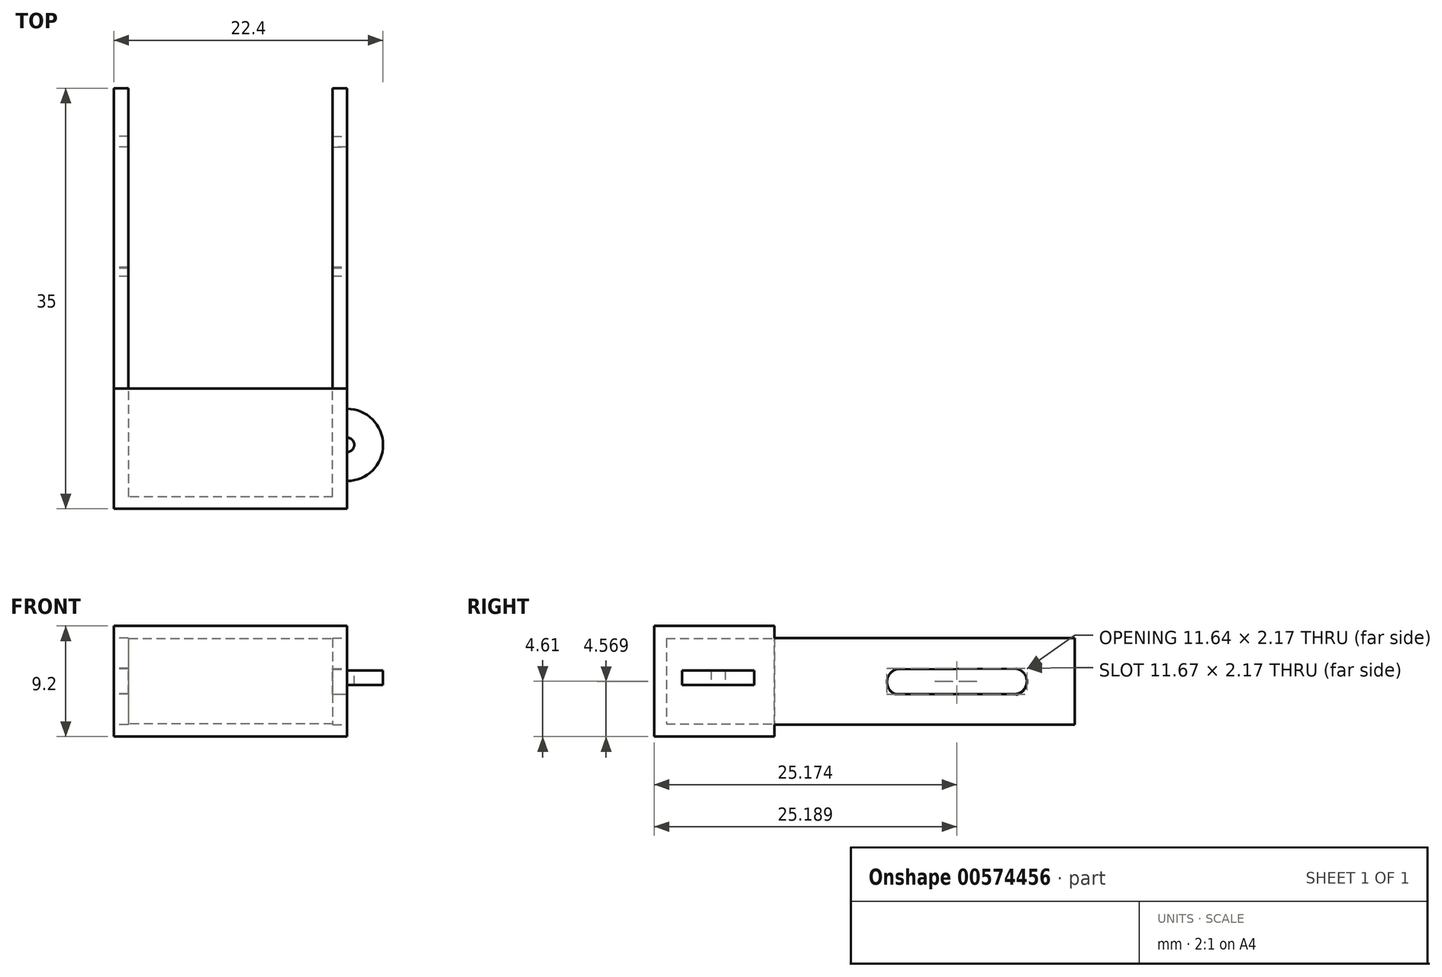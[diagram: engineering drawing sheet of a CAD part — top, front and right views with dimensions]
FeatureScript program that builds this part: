
annotation { "Feature Type Name" : "Feature", "Feature Type Description" : "" }
export const myFeature = defineFeature(function(context is Context, id is Id, definition is map)
    precondition{}
    {
        {
            var Q0;
            Q0=qCreatedBy(makeId("Right.planeOp"),FACE);
            var sketch = newSketch(context, id + "F0", { "sketchPlane" : qUnion([Q0])});
            skLineSegment(sketch, "E0.bottom", {"start": v(-18.67, 6.84) * mm, "end": v(-8.67, 6.84) * mm});
            skLineSegment(sketch, "E0.top", {"start": v(-18.67, -2.36) * mm, "end": v(-8.67, -2.36) * mm});
            skLineSegment(sketch, "E0.left", {"start": v(-18.67, 6.84) * mm, "end": v(-18.67, -2.36) * mm});
            skLineSegment(sketch, "E0.right", {"start": v(-8.67, 6.84) * mm, "end": v(-8.67, -2.36) * mm});
            skPoint(sketch, "E1", {"position": v(-8.67, 2.24) * mm});
            skLineSegment(sketch, "E2", {"start": v(-8.67, 2.24) * mm, "end": v(-8.67, 5.84) * mm});
            skLineSegment(sketch, "E3", {"start": v(-8.67, 5.84) * mm, "end": v(16.33, 5.84) * mm});
            skLineSegment(sketch, "E4", {"start": v(16.33, 5.84) * mm, "end": v(16.33, -1.36) * mm});
            skLineSegment(sketch, "E5", {"start": v(16.33, -1.36) * mm, "end": v(-8.67, -1.36) * mm});
            skPoint(sketch, "E6", {"position": v(11.33, 2.27) * mm});
            skPoint(sketch, "E7", {"position": v(1.33, 2.27) * mm});
            skLineSegment(sketch, "E8", {"start": v(1.44, 3.27) * mm, "end": v(11.43, 3.33) * mm});
            skLineSegment(sketch, "E9", {"start": v(11.43, 3.33) * mm, "end": v(11.43, 1.17) * mm});
            skLineSegment(sketch, "E10", {"start": v(11.43, 1.17) * mm, "end": v(1.33, 1.2) * mm});
            skArc(sketch, "E11", {"start": v(1.44, 3.27) * mm, "mid": v(0.67, 2.28) * mm, "end": v(1.33, 1.2) * mm});
            skArc(sketch, "E12", {"start": v(11.43, 1.17) * mm, "mid": v(12.34, 2.25) * mm, "end": v(11.43, 3.33) * mm});
            skLineSegment(sketch, "E13.top", {"start": v(-8.67, -1.36) * mm, "end": v(16.33, -1.36) * mm});
            skLineSegment(sketch, "E13.left", {"start": v(-8.67, 6.84) * mm, "end": v(-8.67, -1.36) * mm});
            skSolve(sketch);
        }
        {
            var Q0;
            {var subQ1=sQuery(id+"F0.wireOp",EDGE,"E0.bottom");Q0=makeQuery(id+"F0.imprint","IMPRINT",FACE,{"disambiguationData":[TD([[makeQuery(id+"F0.imprint","IMPRINT",EDGE,{"derivedFrom":subQ1}),-1.0]])]});}
            extrude(context, id + "F1", {"entities" : qUnion([Q0]), "depth" : 19.4 * mm, "offsetDistance" : 25 * mm});
        }
        {
            var Q0;
            Q0 = qSketchRegion(id + "F0", true);
            extrude(context, id + "F2", {"entities" : qUnion([Q0]), "operationType" : NewBodyOperationType.ADD, "depth" : 1.2 * mm, "offsetDistance" : 25 * mm});
        }
        {
            var Q0;
            Q0=makeQuery(id+"F1.opExtrude","CAP_FACE",FACE,{"disambiguationData":[OSD([sQuery(id+"F0.wireOp",EDGE,"E0.bottom"),sQuery(id+"F0.wireOp",EDGE,"E0.top"),sQuery(id+"F0.wireOp",EDGE,"E0.left"),sQuery(id+"F0.wireOp",EDGE,"E0.right"),sQuery(id+"F0.wireOp",EDGE,"E13.left")])],"isStart":false});
            var sketch = newSketch(context, id + "F3", { "sketchPlane" : qUnion([Q0])});
            skPoint(sketch, "E14", {"position": v(-8.67, 6.84) * mm});
            skPoint(sketch, "E15", {"position": v(-8.67, 5.84) * mm});
            skLineSegment(sketch, "E16", {"start": v(-8.67, 5.84) * mm, "end": v(16.33, 5.84) * mm});
            skLineSegment(sketch, "E17", {"start": v(16.33, 5.84) * mm, "end": v(16.33, -1.36) * mm});
            skLineSegment(sketch, "E18", {"start": v(16.33, -1.36) * mm, "end": v(-8.67, -1.36) * mm});
            skLineSegment(sketch, "E19", {"start": v(-8.67, -1.36) * mm, "end": v(-8.67, 5.84) * mm});
            skPoint(sketch, "E20", {"position": v(10.79, 2.26) * mm});
            skPoint(sketch, "E21", {"position": v(1.25, 2.26) * mm});
            skLineSegment(sketch, "E22", {"start": v(1.47, 3.23) * mm, "end": v(11.47, 3.3) * mm});
            skLineSegment(sketch, "E23", {"start": v(11.43, 3.3) * mm, "end": v(11.43, 1.13) * mm});
            skLineSegment(sketch, "E24", {"start": v(11.47, 1.13) * mm, "end": v(1.36, 1.17) * mm});
            skArc(sketch, "E25", {"start": v(1.47, 3.23) * mm, "mid": v(0.7, 2.24) * mm, "end": v(1.36, 1.17) * mm});
            skArc(sketch, "E26", {"start": v(11.43, 1.13) * mm, "mid": v(12.34, 2.2) * mm, "end": v(11.43, 3.3) * mm});
            skSolve(sketch);
        }
        {
            var Q0;
            Q0=makeQuery(id+"F3.imprint","IMPRINT",FACE,{"disambiguationData":[TD([[makeQuery(id+"F3.imprint","IMPRINT",EDGE,{"derivedFrom":sQuery(id+"F3.wireOp",EDGE,"E16")}),-1.0]])]});
            extrude(context, id + "F4", {"entities" : qUnion([Q0]), "operationType" : NewBodyOperationType.ADD, "oppositeDirection" : true, "depth" : 1.2 * mm, "offsetDistance" : 25 * mm});
        }
        {
            var Q0;
            Q0=makeQuery(id+"F1.opExtrude","SWEPT_FACE",FACE,{"disambiguationData":[OSD([sQuery(id+"F0.wireOp",EDGE,"E0.right"),sQuery(id+"F0.wireOp",EDGE,"E13.left")])]});
            var sketch = newSketch(context, id + "F5", { "sketchPlane" : qUnion([Q0])});
            skLineSegment(sketch, "E27", {"start": v(-18.35, -1.31) * mm, "end": v(-1.25, -1.31) * mm});
            skLineSegment(sketch, "E28", {"start": v(-1.25, -1.31) * mm, "end": v(-1.25, 5.79) * mm});
            skLineSegment(sketch, "E29", {"start": v(-1.25, 5.79) * mm, "end": v(-18.35, 5.79) * mm});
            skLineSegment(sketch, "E30", {"start": v(-18.35, 5.79) * mm, "end": v(-18.35, -1.31) * mm});
            skSolve(sketch);
        }
        {
            var Q0;
            {var subQ0=sQuery(id+"F5.wireOp",EDGE,"E28");Q0=makeQuery(id+"F5.imprint","IMPRINT",FACE,{"disambiguationData":[TD([[makeQuery(id+"F5.imprint","IMPRINT",EDGE,{"derivedFrom":subQ0}),1.0]])]});}
            extrude(context, id + "F6", {"entities" : qUnion([Q0]), "operationType" : NewBodyOperationType.REMOVE, "oppositeDirection" : true, "depth" : 9 * mm, "offsetDistance" : 25 * mm});
        }
        {
            var Q0;
            Q0=makeQuery(id+"F4.boolean.opBoolean","MERGE",FACE,{"derivedFrom":[makeQuery(id+"F1.opExtrude","CAP_FACE",FACE,{"disambiguationData":[OSD([sQuery(id+"F0.wireOp",EDGE,"E0.bottom"),sQuery(id+"F0.wireOp",EDGE,"E0.top"),sQuery(id+"F0.wireOp",EDGE,"E0.left"),sQuery(id+"F0.wireOp",EDGE,"E0.right"),sQuery(id+"F0.wireOp",EDGE,"E13.left")])],"isStart":false}),makeQuery(id+"F4.opExtrude","CAP_FACE",FACE,{"disambiguationData":[OSD([sQuery(id+"F3.wireOp",EDGE,"E16"),sQuery(id+"F3.wireOp",EDGE,"E17"),sQuery(id+"F3.wireOp",EDGE,"E18"),sQuery(id+"F3.wireOp",EDGE,"E19"),sQuery(id+"F3.wireOp",EDGE,"E22"),sQuery(id+"F3.wireOp",EDGE,"E23"),sQuery(id+"F3.wireOp",EDGE,"E24"),sQuery(id+"F3.wireOp",EDGE,"E25"),sQuery(id+"F3.wireOp",EDGE,"E26")])],"isStart":true})]});
            var sketch = newSketch(context, id + "F7", { "sketchPlane" : qUnion([Q0])});
            skLineSegment(sketch, "E31.bottom", {"start": v(-12.75, 3.14) * mm, "end": v(-10.35, 3.14) * mm});
            skLineSegment(sketch, "E31.top", {"start": v(-12.75, 1.94) * mm, "end": v(-10.35, 1.94) * mm});
            skLineSegment(sketch, "E31.left", {"start": v(-12.75, 3.14) * mm, "end": v(-12.75, 1.94) * mm});
            skLineSegment(sketch, "E31.right", {"start": v(-10.35, 3.14) * mm, "end": v(-10.35, 1.94) * mm});
            skLineSegment(sketch, "E32.bottom", {"start": v(-12.75, 3.14) * mm, "end": v(-13.35, 3.14) * mm});
            skLineSegment(sketch, "E32.top", {"start": v(-12.75, 1.94) * mm, "end": v(-13.35, 1.94) * mm});
            skLineSegment(sketch, "E32.right", {"start": v(-13.35, 3.14) * mm, "end": v(-13.35, 1.94) * mm});
            skLineSegment(sketch, "E33", {"start": v(-13.35, 3.14) * mm, "end": v(-13.35, 1.94) * mm, "construction": true});
            skSolve(sketch);
        }
        {
            var Q0;
            Q0=makeQuery(id+"F7.imprint","IMPRINT",FACE,{"disambiguationData":[TD([[makeQuery(id+"F7.imprint","IMPRINT",EDGE,{"derivedFrom":sQuery(id+"F7.wireOp",EDGE,"E31.bottom")}),-1.0]])]});
            var Q1;
            Q1=sQuery(id+"F7.wireOp",EDGE,"E32.right");
            revolve(context, id + "F8", {"operationType" : NewBodyOperationType.ADD, "entities" : qUnion([Q0]), "axis" : qUnion([Q1]), "revolveType" : RevolveType.ONE_DIRECTION, "angle" : 180 * degree});
        }
    });
